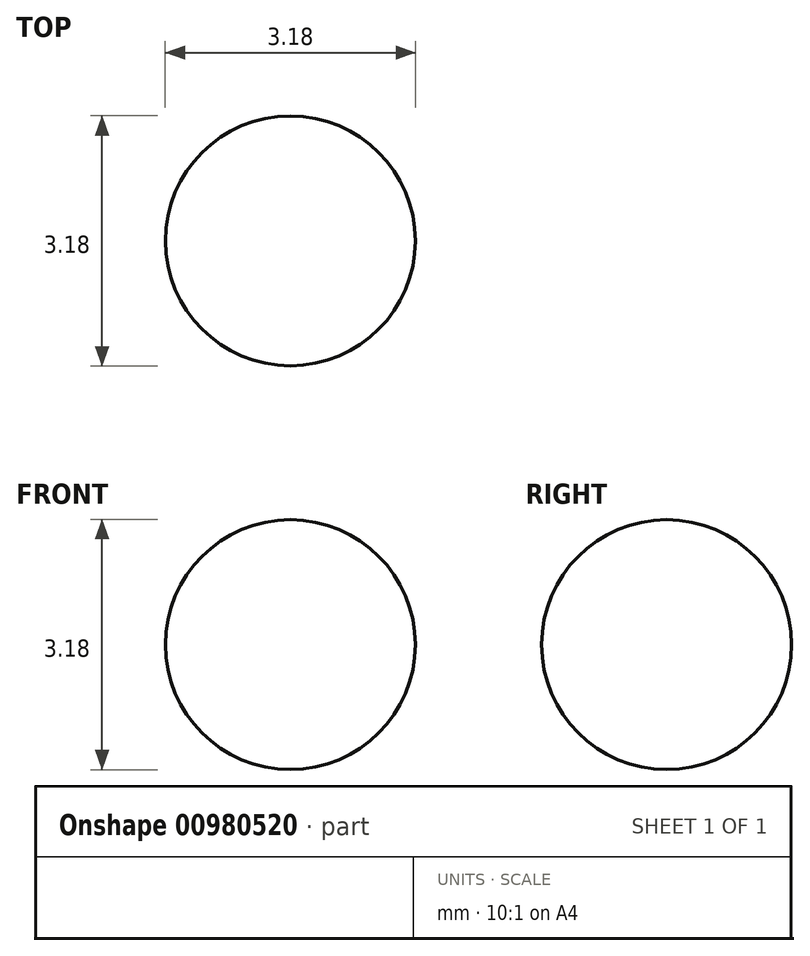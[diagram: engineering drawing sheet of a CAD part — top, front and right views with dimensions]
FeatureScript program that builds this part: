
annotation { "Feature Type Name" : "Feature", "Feature Type Description" : "" }
export const myFeature = defineFeature(function(context is Context, id is Id, definition is map)
    precondition{}
    {
        {
            var Q0;
            Q0=qCreatedBy(makeId("Front.planeOp"),FACE);
            var sketch = newSketch(context, id + "F0", { "sketchPlane" : qUnion([Q0])});
            skArc(sketch, "E0", {"start": v(0, 1.59) * mm, "mid": v(-1.59, 0) * mm, "end": v(0, -1.59) * mm});
            skLineSegment(sketch, "E1", {"start": v(0, 1.59) * mm, "end": v(0, -1.59) * mm});
            skSolve(sketch);
        }
        {
            var Q0;
            Q0=makeQuery(id+"F0.imprint","IMPRINT",FACE,{"disambiguationData":[TD([[makeQuery(id+"F0.imprint","IMPRINT",EDGE,{"derivedFrom":sQuery(id+"F0.wireOp",EDGE,"E0")}),1.0]])]});
            var Q1;
            Q1=sQuery(id+"F0.wireOp",EDGE,"E1");
            revolve(context, id + "F1", {"surfaceOperationType" : NewSurfaceOperationType.NEW, "entities" : qUnion([Q0]), "axis" : qUnion([Q1]), "revolveType" : RevolveType.FULL});
        }
    });
